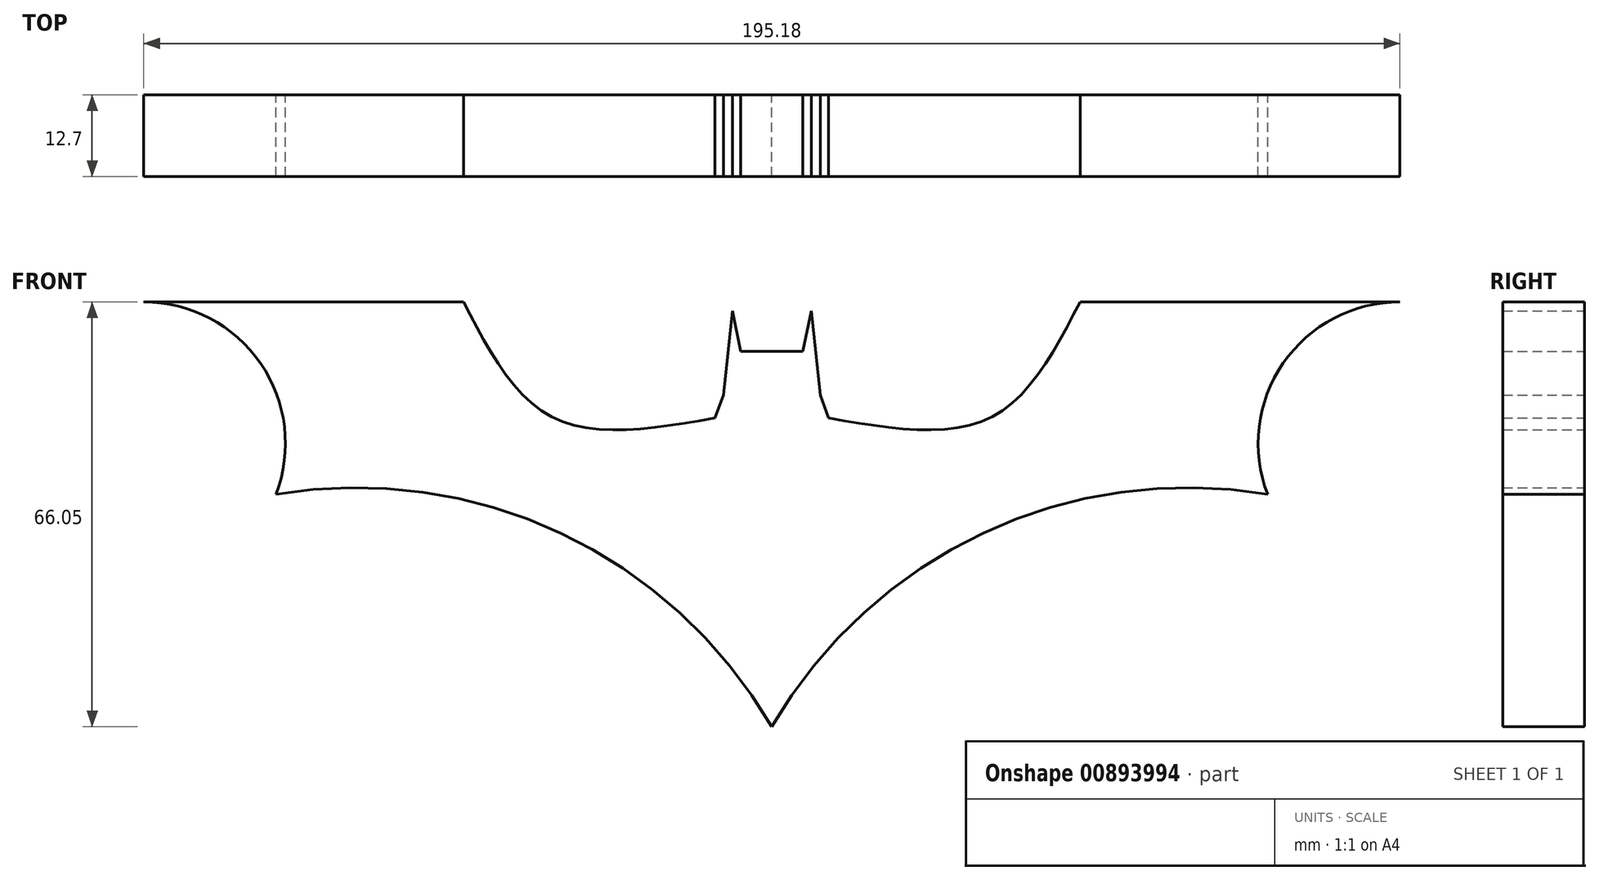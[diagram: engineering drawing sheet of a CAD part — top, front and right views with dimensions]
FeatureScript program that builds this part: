
annotation { "Feature Type Name" : "Feature", "Feature Type Description" : "" }
export const myFeature = defineFeature(function(context is Context, id is Id, definition is map)
    precondition{}
    {
        {
            var Q0;
            Q0=qCreatedBy(makeId("Front.planeOp"),FACE);
            var sketch = newSketch(context, id + "F0", { "sketchPlane" : qUnion([Q0])});
            skLineSegment(sketch, "E0", {"start": v(0, -50.24) * mm, "end": v(0, 60.92) * mm, "construction": true});
            skLineSegment(sketch, "E1", {"start": v(0, 41.3) * mm, "end": v(-4.83, 41.3) * mm});
            skLineSegment(sketch, "E2", {"start": v(-4.83, 41.3) * mm, "end": v(-6.13, 47.59) * mm});
            skLineSegment(sketch, "E3", {"start": v(-6.13, 47.59) * mm, "end": v(-7.54, 34.49) * mm});
            skLineSegment(sketch, "E4", {"start": v(-7.54, 34.49) * mm, "end": v(-8.84, 30.91) * mm});
            skFitSpline(sketch, "E5", {"points": [v(-8.84, 30.91) * mm, v(-33.86, 30.91) * mm, v(-47.9, 48.96) * mm], "startDerivative": vector(-54.1, -9.44) * mm, "endDerivative": vector(-23.8, 45.95) * mm});
            skLineSegment(sketch, "E6", {"start": v(-47.9, 48.96) * mm, "end": v(-97.6, 48.96) * mm});
            skArc(sketch, "E7", {"start": v(-77.04, 19.04) * mm, "mid": v(-79.45, 39.4) * mm, "end": v(-97.6, 48.96) * mm});
            skArc(sketch, "E8", {"start": v(0, -17.1) * mm, "mid": v(-32.87, 13.03) * mm, "end": v(-77.04, 19.04) * mm});
            skLineSegment(sketch, "E9.MirrorCS", {"start": v(0, 41.3) * mm, "end": v(4.83, 41.3) * mm});
            skLineSegment(sketch, "E10.MirrorCS", {"start": v(4.83, 41.3) * mm, "end": v(6.13, 47.59) * mm});
            skLineSegment(sketch, "E11.MirrorCS", {"start": v(6.13, 47.59) * mm, "end": v(7.54, 34.49) * mm});
            skArc(sketch, "E12.MirrorCS", {"start": v(77.04, 19.04) * mm, "mid": v(79.45, 39.4) * mm, "end": v(97.6, 48.96) * mm});
            skArc(sketch, "E13.MirrorCS", {"start": v(0, -17.1) * mm, "mid": v(32.87, 13.03) * mm, "end": v(77.04, 19.04) * mm});
            skLineSegment(sketch, "E14.MirrorCS", {"start": v(47.9, 48.96) * mm, "end": v(97.6, 48.96) * mm});
            skFitSpline(sketch, "E15.MirrorCS", {"points": [v(8.84, 30.91) * mm, v(33.86, 30.91) * mm, v(47.9, 48.96) * mm], "startDerivative": vector(54.1, -9.44) * mm, "endDerivative": vector(23.8, 45.95) * mm});
            skLineSegment(sketch, "E16.MirrorCS", {"start": v(7.54, 34.49) * mm, "end": v(8.84, 30.91) * mm});
            skSolve(sketch);
        }
        {
            var Q0;
            Q0 = qSketchRegion(id + "F0", true);
            extrude(context, id + "F1", {"entities" : qUnion([Q0]), "depth" : 12.7 * mm, "offsetDistance" : 25.4 * mm});
        }
    });
